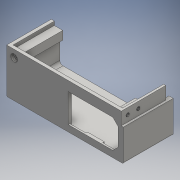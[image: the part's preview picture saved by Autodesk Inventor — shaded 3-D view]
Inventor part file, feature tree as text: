
AUTODESK INVENTOR PART (.ipt)
format: ipt  version: 2016 (Build 200138000, 138)  size: 679,424 bytes
history: native  units: mm
features: extrude x7, sketch x7, projected_geometry x6, other x2, fillet x2
ambient origin geometry x8: Origin, YZ Plane, XZ Plane, XY Plane, X Axis, Y Axis, Z Axis, Center Point
bodies: Solid1 (feature_tree)
feature tree (24):
  other  "psu_cover_20a_i3_steel"
  other  "MeshFeature1"
  extrude  "Extrusion1"  Depth=10.0mm TaperAngle=0.0deg
  extrude  "Extrusion2"  Depth=27.0mm
  extrude  "Extrusion3"  Depth=6.0mm
  extrude  "Extrusion4"  Depth=5.0mm
  extrude  "Extrusion5"  Depth=5.0mm
  fillet  "Fillet1"  Radius=10.0mm
  fillet  "Fillet2"  Radius=10.0mm
  extrude  "Extrusion6"  Depth=10.0mm TaperAngle=0.0deg
  extrude  "Extrusion7"  Depth=1.0mm
  sketch  "Sketch1"  dims[d0=10.0mm d1=0.0mm d2=10.0mm d3=0.0mm]
  projected_geometry  "Projected Loop1"
  sketch  "Sketch2"  dims[d4=47.0mm d5=27.0mm]
  projected_geometry  "Projected Loop2"
  sketch  "Sketch3"  dims[d6=5.0mm d7=6.0mm]
  sketch  "Sketch4"  dims[d8=5.0mm d9=5.0mm]
  projected_geometry  "Projected Loop3"
  sketch  "Sketch5"  dims[d10=5.0mm d11=5.0mm d12=10.0mm d13=0.0mm d14=10.0mm d15=0.0mm]
  projected_geometry  "Projected Loop4"
  sketch  "Sketch6"  dims[d16=14.0mm d17=10.0mm d18=0.0mm]
  projected_geometry  "Projected Loop5"
  sketch  "Sketch7"  dims[d19=3.0mm d20=1.0mm d21=1.5mm d22=15.0mm d23=15.0mm d24=11.0mm d25=11.0mm d26=1.5mm d27=0.0mm d28=10.0mm d29=0.0mm]
  projected_geometry  "Projected Loop6"
